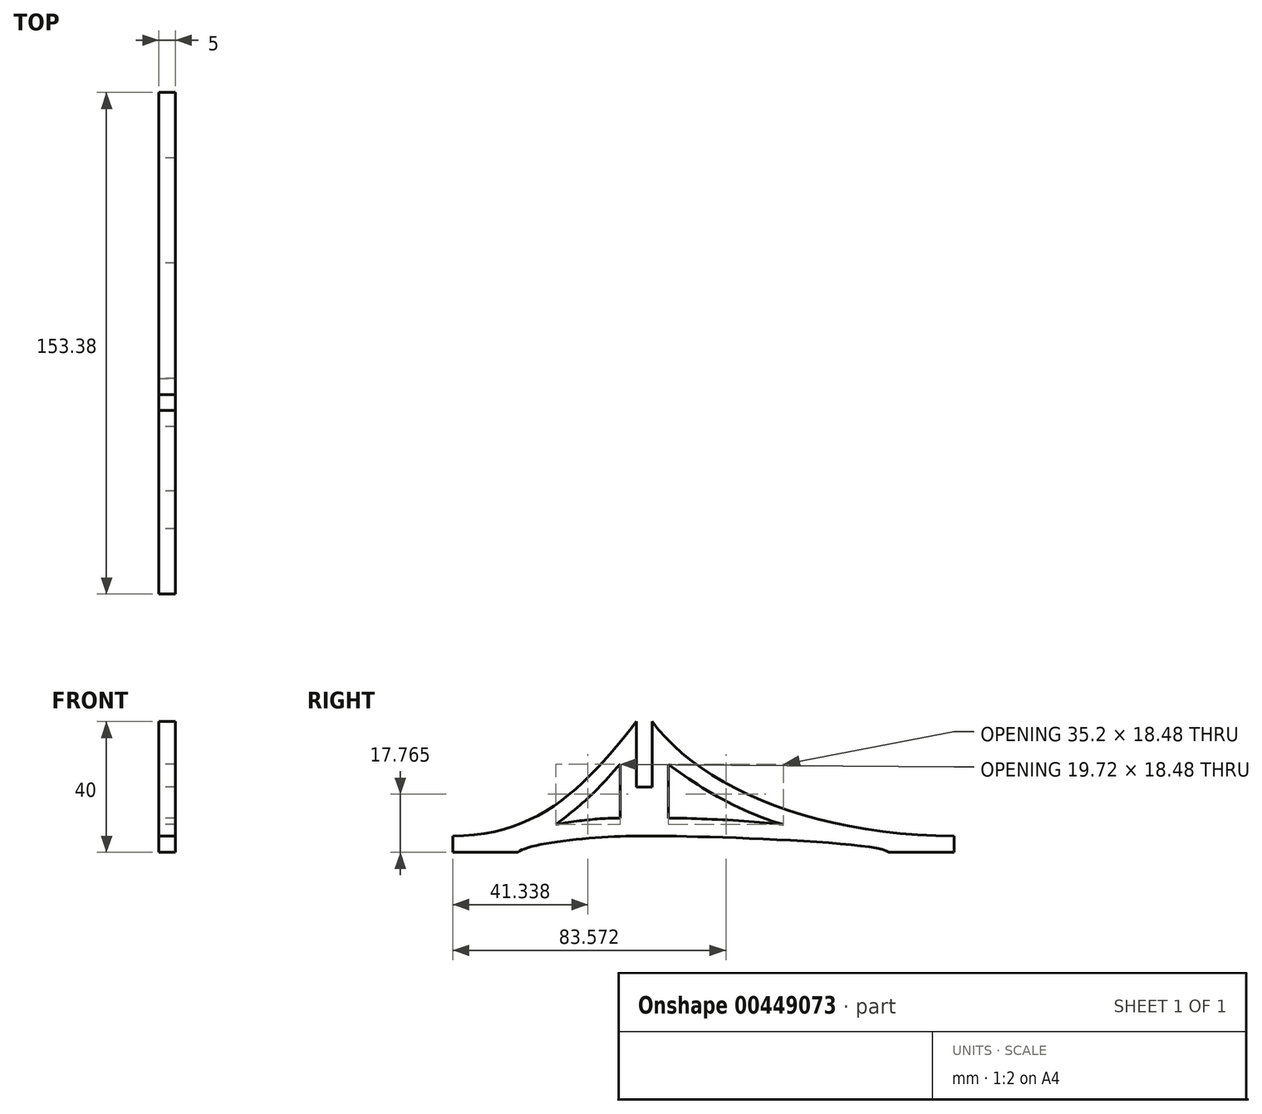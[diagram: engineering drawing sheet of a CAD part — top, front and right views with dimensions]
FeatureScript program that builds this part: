
annotation { "Feature Type Name" : "Feature", "Feature Type Description" : "" }
export const myFeature = defineFeature(function(context is Context, id is Id, definition is map)
    precondition{}
    {
        {
            var Q0;
            Q0=qCreatedBy(makeId("Right.planeOp"),FACE);
            var sketch = newSketch(context, id + "F0", { "sketchPlane" : qUnion([Q0])});
            skLineSegment(sketch, "E0.bottom", {"start": v(0, 0) * mm, "end": v(2.4, 0) * mm});
            skLineSegment(sketch, "E0.top", {"start": v(0, 40) * mm, "end": v(2.4, 40) * mm});
            skLineSegment(sketch, "E0.left", {"start": v(0, 0) * mm, "end": v(0, 40) * mm});
            skLineSegment(sketch, "E0.right", {"start": v(2.4, 0) * mm, "end": v(2.4, 40) * mm});
            skLineSegment(sketch, "E1", {"start": v(2.4, 0) * mm, "end": v(94.8, 0) * mm});
            skLineSegment(sketch, "E2", {"start": v(94.8, 0) * mm, "end": v(94.8, 5) * mm});
            skFitSpline(sketch, "E3", {"points": [v(2.4, 40) * mm, v(94.8, 5) * mm], "startDerivative": vector(42.66, -58.23) * mm, "endDerivative": vector(130.97, 0) * mm});
            skLineSegment(sketch, "E4.bottom", {"start": v(2.4, 0) * mm, "end": v(0, 0) * mm});
            skLineSegment(sketch, "E4.top", {"start": v(2.4, 20) * mm, "end": v(0, 20) * mm});
            skLineSegment(sketch, "E4.left", {"start": v(2.4, 0) * mm, "end": v(2.4, 20) * mm});
            skLineSegment(sketch, "E4.right", {"start": v(0, 0) * mm, "end": v(0, 20) * mm});
            skLineSegment(sketch, "E5.MirrorCS", {"start": v(0, 0) * mm, "end": v(-2.4, 0) * mm});
            skLineSegment(sketch, "E6.MirrorCS", {"start": v(-2.4, 0) * mm, "end": v(0, 0) * mm});
            skLineSegment(sketch, "E7.MirrorCS", {"start": v(0, 40) * mm, "end": v(-2.4, 40) * mm});
            skLineSegment(sketch, "E8.MirrorCS", {"start": v(-2.4, 20) * mm, "end": v(0, 20) * mm});
            skLineSegment(sketch, "E9.MirrorCS", {"start": v(-2.4, 0) * mm, "end": v(-2.4, 20) * mm});
            skLineSegment(sketch, "E10.MirrorCS", {"start": v(-2.4, 0) * mm, "end": v(-2.4, 40) * mm});
            skLineSegment(sketch, "E11", {"start": v(2.4, 5) * mm, "end": v(2.4, 5) * mm});
            skFitSpline(sketch, "E12", {"points": [v(74.8, 0) * mm, v(2.4, 5) * mm], "startDerivative": vector(-10.23, 10.25) * mm, "endDerivative": vector(-42.28, 0) * mm});
            skLineSegment(sketch, "E13", {"start": v(-2.4, 5) * mm, "end": v(2.4, 5) * mm});
            skLineSegment(sketch, "E14.bottom", {"start": v(-2.4, 0) * mm, "end": v(-7.4, 0) * mm});
            skLineSegment(sketch, "E14.left", {"start": v(-2.4, 0) * mm, "end": v(-2.4, 30.49) * mm});
            skLineSegment(sketch, "E15.bottom", {"start": v(-7.4, 0) * mm, "end": v(-58.58, 0) * mm});
            skLineSegment(sketch, "E15.right", {"start": v(-58.58, 0) * mm, "end": v(-58.58, 5) * mm});
            skFitSpline(sketch, "E16", {"points": [v(-2.4, 5) * mm, v(-38.58, 0) * mm], "startDerivative": vector(-34.54, 0) * mm, "endDerivative": vector(-8.24, -8.56) * mm});
            skFitSpline(sketch, "E17", {"points": [v(-58.58, 5) * mm, v(-2.4, 40) * mm], "startDerivative": vector(78.33, 0) * mm, "endDerivative": vector(47.1, 60.35) * mm});
            skFitSpline(sketch, "E18", {"points": [v(7.4, 27) * mm, v(7.4, 10.45) * mm], "startDerivative": vector(0.08, -16.13) * mm, "endDerivative": vector(0.08, -16.13) * mm});
            skFitSpline(sketch, "E19", {"points": [v(7.4, 10.45) * mm, v(42.6, 8.52) * mm], "startDerivative": vector(29.85, -0.04) * mm, "endDerivative": vector(31.8, -3.48) * mm});
            skFitSpline(sketch, "E20", {"points": [v(42.6, 8.52) * mm, v(7.4, 27) * mm], "startDerivative": vector(-41.03, 11.36) * mm, "endDerivative": vector(-26.1, 20.27) * mm});
            skFitSpline(sketch, "E21", {"points": [v(-7.4, 27) * mm, v(-7.4, 10.45) * mm], "startDerivative": vector(-0.18, -16.55) * mm, "endDerivative": vector(-0.18, -16.55) * mm});
            skFitSpline(sketch, "E22", {"points": [v(-7.4, 27) * mm, v(-27.1, 8.52) * mm], "startDerivative": vector(-22.64, -26.02) * mm, "endDerivative": vector(-25.26, -18.85) * mm});
            skFitSpline(sketch, "E23", {"points": [v(-27.1, 8.52) * mm, v(-7.4, 10.45) * mm], "startDerivative": vector(23.65, 3.8) * mm, "endDerivative": vector(22.35, 0.13) * mm});
            skSolve(sketch);
        }
        {
            var Q0;
            Q0=makeQuery(id+"F0.imprint","IMPRINT",FACE,{"disambiguationData":[TD([[makeQuery(id+"F0.imprint","IMPRINT",EDGE,{"derivedFrom":sQuery(id+"F0.wireOp",EDGE,"E15.top")}),1.0]])]});
            var Q1;
            {var subQ0=sQuery(id+"F0.wireOp",EDGE,"E8.MirrorCS");Q1=makeQuery(id+"F0.imprint","IMPRINT",FACE,{"disambiguationData":[TD([[makeQuery(id+"F0.imprint","IMPRINT",EDGE,{"derivedFrom":subQ0}),-1.0]])]});}
            var Q2;
            {var subQ0=sQuery(id+"F0.wireOp",EDGE,"E4.top");Q2=makeQuery(id+"F0.imprint","IMPRINT",FACE,{"disambiguationData":[TD([[makeQuery(id+"F0.imprint","IMPRINT",EDGE,{"derivedFrom":subQ0}),1.0]])]});}
            var Q3;
            {var subQ3=sQuery(id+"F0.wireOp",EDGE,"E0.right");Q3=makeQuery(id+"F0.imprint","IMPRINT",FACE,{"disambiguationData":[TD([[makeQuery(id+"F0.imprint","IMPRINT",EDGE,{"derivedFrom":subQ3}),-1.0]])]});}
            var Q4;
            {var subQ4=sQuery(id+"F0.wireOp",EDGE,"E10.MirrorCS");Q4=makeQuery(id+"F0.imprint","IMPRINT",FACE,{"disambiguationData":[TD([[makeQuery(id+"F0.imprint","IMPRINT",EDGE,{"derivedFrom":subQ4}),1.0]])]});}
            extrude(context, id + "F1", {"entities" : qUnion([Q0, Q1, Q2, Q3, Q4]), "depth" : 5 * mm});
        }
    });
